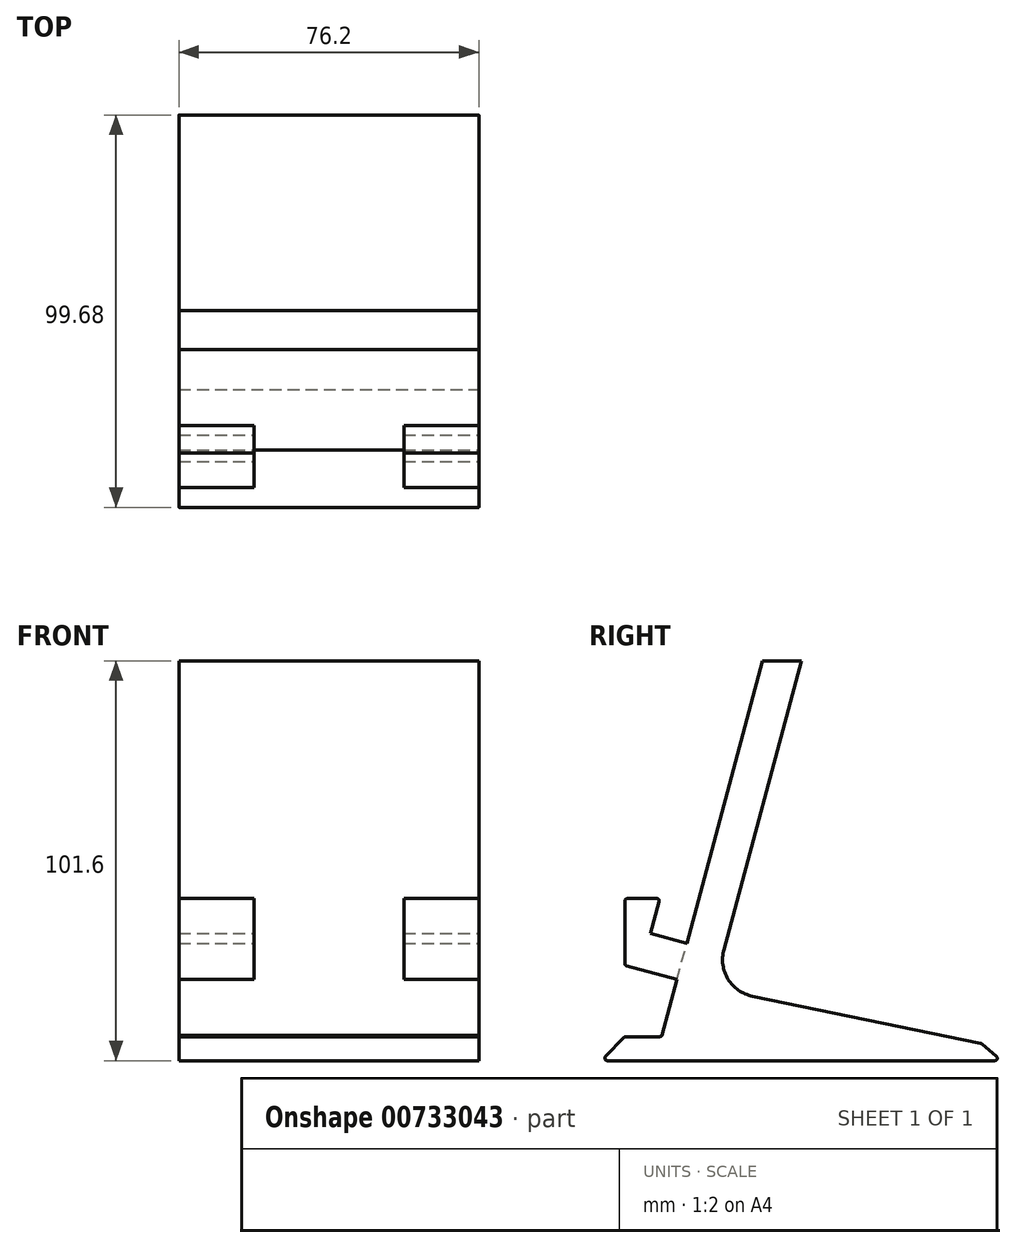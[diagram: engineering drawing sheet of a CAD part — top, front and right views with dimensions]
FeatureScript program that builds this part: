
annotation { "Feature Type Name" : "Feature", "Feature Type Description" : "" }
export const myFeature = defineFeature(function(context is Context, id is Id, definition is map)
    precondition{}
    {
        {
            var Q0;
            Q0=qCreatedBy(makeId("Top.planeOp"),FACE);
            var sketch = newSketch(context, id + "F0", { "sketchPlane" : qUnion([Q0])});
            skLineSegment(sketch, "E0.bottom", {"start": v(-38.1, 50.8) * mm, "end": v(38.1, 50.8) * mm});
            skLineSegment(sketch, "E0.top", {"start": v(-38.1, -50.8) * mm, "end": v(38.1, -50.8) * mm});
            skLineSegment(sketch, "E0.left", {"start": v(-38.1, 50.8) * mm, "end": v(-38.1, -50.8) * mm});
            skLineSegment(sketch, "E0.right", {"start": v(38.1, 50.8) * mm, "end": v(38.1, -50.8) * mm});
            skPoint(sketch, "E0.middle", {"position": v(0, 0) * mm});
            skSolve(sketch);
        }
        {
            var Q0;
            Q0 = qSketchRegion(id + "F0", true);
            extrude(context, id + "F1", {"entities" : qUnion([Q0]), "depth" : 101.6 * mm, "offsetDistance" : 25.4 * mm});
        }
        {
            var Q0;
            Q0=makeQuery(id+"F1.opExtrude","SWEPT_FACE",FACE,{"disambiguationData":[OSD([sQuery(id+"F0.wireOp",EDGE,"E0.right")])]});
            var sketch = newSketch(context, id + "F2", { "sketchPlane" : qUnion([Q0])});
            skLineSegment(sketch, "E1", {"start": v(0, 101.6) * mm, "end": v(-19.72, 28.17) * mm});
            skLineSegment(sketch, "E2", {"start": v(-12.44, 16.37) * mm, "end": v(45.52, 4.46) * mm});
            skLineSegment(sketch, "E3", {"start": v(45.8, 4.32) * mm, "end": v(49.52, 1.1) * mm});
            skLineSegment(sketch, "E4", {"start": v(50.8, 0) * mm, "end": v(50.8, 101.6) * mm});
            skLineSegment(sketch, "E5", {"start": v(50.8, 101.6) * mm, "end": v(0, 101.6) * mm});
            skLineSegment(sketch, "E6", {"start": v(-9.86, 101.6) * mm, "end": v(-29.15, 29.8) * mm});
            skLineSegment(sketch, "E7", {"start": v(-29.15, 29.8) * mm, "end": v(-38.35, 32.28) * mm});
            skLineSegment(sketch, "E8", {"start": v(-38.35, 32.28) * mm, "end": v(-36.17, 40.4) * mm});
            skLineSegment(sketch, "E9", {"start": v(-36.77, 41.19) * mm, "end": v(-44.24, 41.19) * mm});
            skLineSegment(sketch, "E10", {"start": v(-44.86, 40.56) * mm, "end": v(-44.86, 24.65) * mm});
            skLineSegment(sketch, "E11", {"start": v(-44.4, 24.04) * mm, "end": v(-32.4, 20.82) * mm});
            skLineSegment(sketch, "E12", {"start": v(-35.99, 6.1) * mm, "end": v(-44.6, 6.1) * mm});
            skLineSegment(sketch, "E13", {"start": v(-45.05, 5.92) * mm, "end": v(-49.76, 1.06) * mm});
            skPoint(sketch, "E14.visualSharp", {"position": v(-22.35, 18.4) * mm});
            skArc(sketch, "E14.filletArc", {"start": v(-19.72, 28.17) * mm, "mid": v(-18.63, 20.7) * mm, "end": v(-12.44, 16.37) * mm});
            skLineSegment(sketch, "E15", {"start": v(-9.86, 101.6) * mm, "end": v(0, 101.6) * mm});
            skLineSegment(sketch, "E16", {"start": v(-49.32, 0) * mm, "end": v(49.11, 0) * mm});
            skPoint(sketch, "E17.visualSharp", {"position": v(50.8, 0) * mm});
            skArc(sketch, "E17.filletArc", {"start": v(49.11, 0) * mm, "mid": v(49.7, 0.4) * mm, "end": v(49.52, 1.1) * mm});
            skPoint(sketch, "E18.visualSharp", {"position": v(45.68, 4.42) * mm});
            skArc(sketch, "E18.filletArc", {"start": v(45.8, 4.32) * mm, "mid": v(45.67, 4.4) * mm, "end": v(45.52, 4.46) * mm});
            skPoint(sketch, "E19.visualSharp", {"position": v(-50.8, 0) * mm});
            skArc(sketch, "E19.filletArc", {"start": v(-49.76, 1.06) * mm, "mid": v(-49.9, 0.38) * mm, "end": v(-49.32, 0) * mm});
            skPoint(sketch, "E20.visualSharp", {"position": v(-44.86, 24.17) * mm});
            skArc(sketch, "E20.filletArc", {"start": v(-44.86, 24.65) * mm, "mid": v(-44.73, 24.27) * mm, "end": v(-44.4, 24.04) * mm});
            skPoint(sketch, "E21.visualSharp", {"position": v(-44.86, 41.19) * mm});
            skArc(sketch, "E21.filletArc", {"start": v(-44.24, 41.19) * mm, "mid": v(-44.68, 41) * mm, "end": v(-44.86, 40.56) * mm});
            skPoint(sketch, "E22.visualSharp", {"position": v(-35.95, 41.19) * mm});
            skArc(sketch, "E22.filletArc", {"start": v(-36.17, 40.4) * mm, "mid": v(-36.27, 40.94) * mm, "end": v(-36.77, 41.19) * mm});
            skPoint(sketch, "E23.visualSharp", {"position": v(-35.95, 6.1) * mm});
            skArc(sketch, "E23.filletArc", {"start": v(-35.99, 6.1) * mm, "mid": v(-35.65, 6.2) * mm, "end": v(-35.42, 6.46) * mm});
            skPoint(sketch, "E24.visualSharp", {"position": v(-44.86, 6.1) * mm});
            skArc(sketch, "E24.filletArc", {"start": v(-44.6, 6.1) * mm, "mid": v(-44.84, 6.06) * mm, "end": v(-45.05, 5.92) * mm});
            skLineSegment(sketch, "E25", {"start": v(-32.4, 20.82) * mm, "end": v(-31.62, 20.6) * mm});
            skLineSegment(sketch, "E26", {"start": v(-31.62, 20.6) * mm, "end": v(-35.42, 6.46) * mm});
            skSolve(sketch);
        }
        {
            var Q0;
            Q0=makeQuery(id+"F2.imprint","IMPRINT",FACE,{"disambiguationData":[TD([[makeQuery(id+"F2.imprint","IMPRINT",EDGE,{"derivedFrom":sQuery(id+"F2.wireOp",EDGE,"E1")}),1.0]])]});
            var Q1;
            {var subQ0=sQuery(id+"F2.wireOp",EDGE,"E6");Q1=makeQuery(id+"F2.imprint","IMPRINT",FACE,{"disambiguationData":[TD([[makeQuery(id+"F2.imprint","IMPRINT",EDGE,{"derivedFrom":subQ0}),-1.0]])]});}
            extrude(context, id + "F3", {"entities" : qUnion([Q0, Q1]), "operationType" : NewBodyOperationType.REMOVE, "endBound" : BoundingType.THROUGH_ALL, "oppositeDirection" : true, "depth" : 25.4 * mm, "offsetDistance" : 25.4 * mm});
        }
        {
            var Q0;
            Q0=makeQuery(id+"F3.boolean.opBoolean","COPY",FACE,{"derivedFrom":makeQuery(id+"F3.opExtrude","SWEPT_FACE",FACE,{"disambiguationData":[OSD([sQuery(id+"F2.wireOp",EDGE,"E6")])]})});
            var sketch = newSketch(context, id + "F4", { "sketchPlane" : qUnion([Q0])});
            skLineSegment(sketch, "E27.bottom", {"start": v(-19.05, 21.23) * mm, "end": v(19.05, 21.23) * mm});
            skLineSegment(sketch, "E27.top", {"start": v(-19.05, 30.31) * mm, "end": v(19.05, 30.31) * mm});
            skLineSegment(sketch, "E27.left", {"start": v(-19.05, 21.23) * mm, "end": v(-19.05, 30.31) * mm});
            skLineSegment(sketch, "E27.right", {"start": v(19.05, 21.23) * mm, "end": v(19.05, 30.31) * mm});
            skSolve(sketch);
        }
        {
            var Q0;
            Q0 = qSketchRegion(id + "F4", true);
            extrude(context, id + "F5", {"entities" : qUnion([Q0]), "operationType" : NewBodyOperationType.REMOVE, "depth" : 25.4 * mm, "offsetDistance" : 25.4 * mm});
        }
        {
            var Q0;
            Q0=makeQuery(id+"F5.boolean.opBoolean","MERGE",FACE,{"derivedFrom":[makeQuery(id+"F3.boolean.opBoolean","COPY",FACE,{"derivedFrom":makeQuery(id+"F3.opExtrude","SWEPT_FACE",FACE,{"disambiguationData":[OSD([sQuery(id+"F2.wireOp",EDGE,"E7")])]})}),makeQuery(id+"F5.opExtrude","SWEPT_FACE",FACE,{"disambiguationData":[OSD([sQuery(id+"F4.wireOp",EDGE,"E27.bottom")])]})]});
            var sketch = newSketch(context, id + "F6", { "sketchPlane" : qUnion([Q0])});
            skLineSegment(sketch, "E28.bottom", {"start": v(-19.05, -52.15) * mm, "end": v(-19.05, -52.15) * mm});
            skLineSegment(sketch, "E28.top", {"start": v(-19.05, -35.88) * mm, "end": v(-19.05, -35.88) * mm});
            skLineSegment(sketch, "E28.left", {"start": v(-19.05, -52.15) * mm, "end": v(-19.05, -35.88) * mm});
            skLineSegment(sketch, "E28.right", {"start": v(-19.05, -52.15) * mm, "end": v(-19.05, -35.88) * mm});
            skLineSegment(sketch, "E29.bottom", {"start": v(19.05, -35.88) * mm, "end": v(19.05, -35.88) * mm});
            skLineSegment(sketch, "E29.top", {"start": v(19.05, -52.15) * mm, "end": v(19.05, -52.15) * mm});
            skLineSegment(sketch, "E29.left", {"start": v(19.05, -35.88) * mm, "end": v(19.05, -52.15) * mm});
            skLineSegment(sketch, "E29.right", {"start": v(19.05, -35.88) * mm, "end": v(19.05, -52.15) * mm});
            skSolve(sketch);
        }
        {
            var Q0;
            {var subQ1=makeQuery(id+"F5.opExtrude","SWEPT_FACE",FACE,{"disambiguationData":[OSD([sQuery(id+"F4.wireOp",EDGE,"E27.bottom")])]});var subQ2=makeQuery(id+"F5.boolean.opBoolean","INTERSECT",EDGE,{"derivedFrom":[makeQuery(id+"F3.boolean.opBoolean","COPY",FACE,{"derivedFrom":makeQuery(id+"F3.opExtrude","SWEPT_FACE",FACE,{"disambiguationData":[OSD([sQuery(id+"F2.wireOp",EDGE,"E10")])]})}),subQ1]});Q0=makeQuery(id+"F6.imprint","IMPRINT",FACE,{"disambiguationData":[TD([[makeQuery(id+"F6.imprint","IMPRINT",EDGE,{"derivedFrom":subQ2}),-1.0]])]});}
            extrude(context, id + "F7", {"entities" : qUnion([Q0]), "operationType" : NewBodyOperationType.REMOVE, "oppositeDirection" : true, "depth" : 19.05 * mm, "offsetDistance" : 25.4 * mm});
        }
    });
